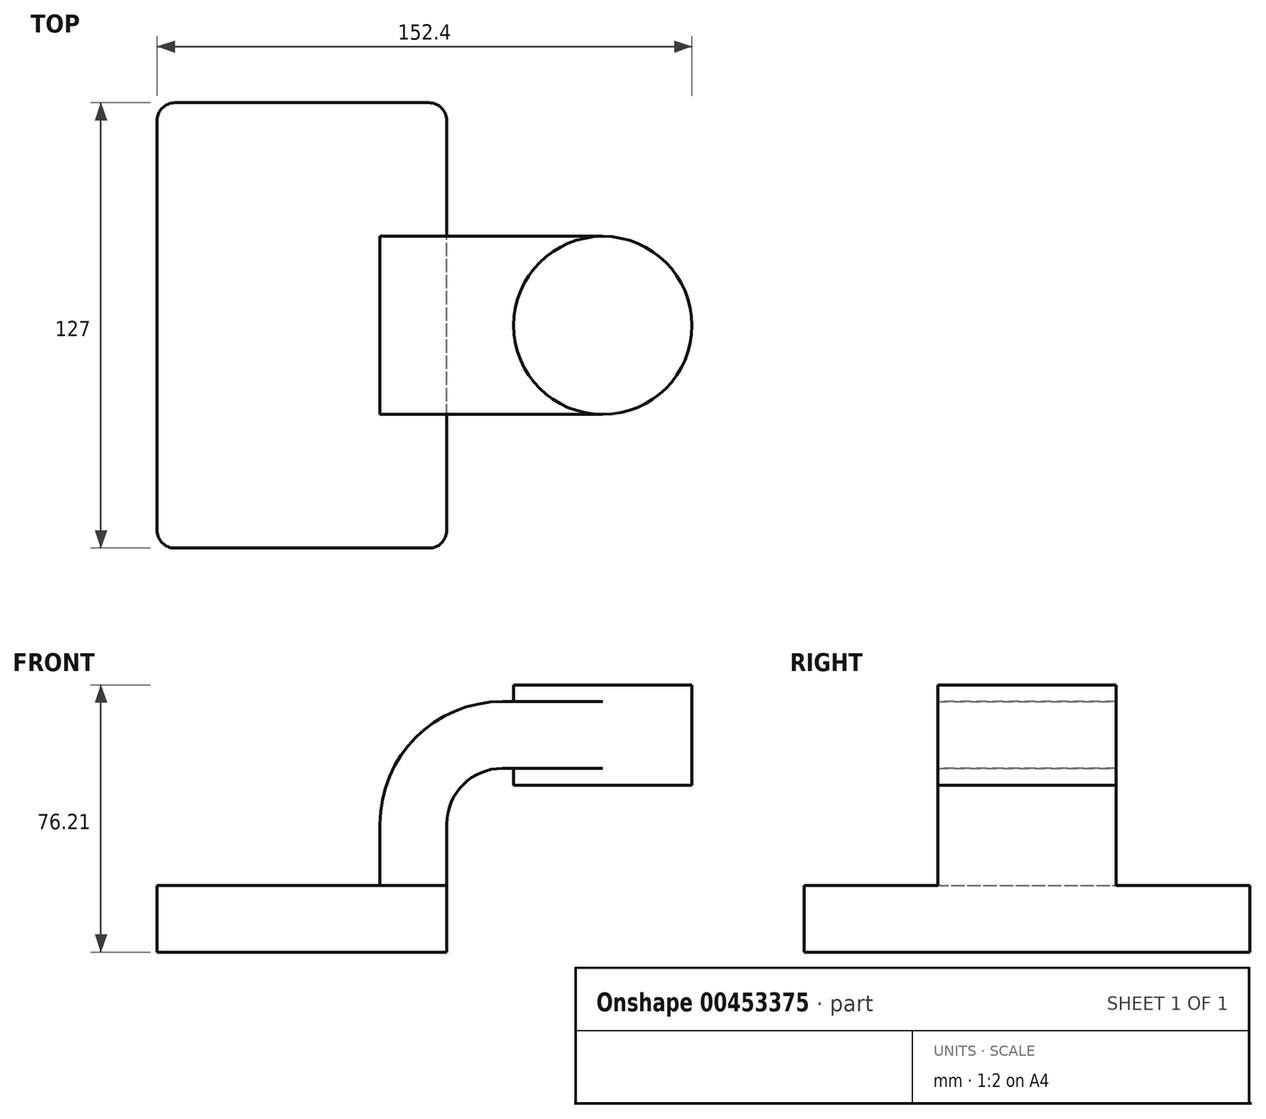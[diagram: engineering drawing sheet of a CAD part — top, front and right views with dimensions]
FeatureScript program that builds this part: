
annotation { "Feature Type Name" : "Feature", "Feature Type Description" : "" }
export const myFeature = defineFeature(function(context is Context, id is Id, definition is map)
    precondition{}
    {
        {
            var Q0;
            Q0=qCreatedBy(makeId("Front.planeOp"),FACE);
            var sketch = newSketch(context, id + "F0", { "sketchPlane" : qUnion([Q0])});
            skLineSegment(sketch, "E0.bottom", {"start": v(-41.28, -9.53) * mm, "end": v(41.28, -9.53) * mm});
            skLineSegment(sketch, "E0.top", {"start": v(-41.28, 9.53) * mm, "end": v(41.28, 9.53) * mm});
            skLineSegment(sketch, "E0.left", {"start": v(-41.28, -9.53) * mm, "end": v(-41.28, 9.53) * mm});
            skLineSegment(sketch, "E0.right", {"start": v(41.28, -9.53) * mm, "end": v(41.28, 9.52) * mm});
            skPoint(sketch, "E0.middle", {"position": v(0, 0) * mm});
            skLineSegment(sketch, "E1.bottom", {"start": v(111.13, 38.1) * mm, "end": v(60.33, 38.1) * mm});
            skLineSegment(sketch, "E1.top", {"start": v(111.13, 66.68) * mm, "end": v(60.33, 66.68) * mm});
            skLineSegment(sketch, "E1.left", {"start": v(111.13, 38.1) * mm, "end": v(111.13, 66.68) * mm});
            skLineSegment(sketch, "E1.right", {"start": v(60.33, 38.1) * mm, "end": v(60.33, 66.67) * mm});
            skPoint(sketch, "E1.middle", {"position": v(85.73, 52.39) * mm});
            skLineSegment(sketch, "E2", {"start": v(41.28, 9.52) * mm, "end": v(41.28, 27) * mm});
            skArc(sketch, "E3", {"start": v(41.27, 27) * mm, "mid": v(45.92, 38.23) * mm, "end": v(57.15, 42.88) * mm});
            skLineSegment(sketch, "E4", {"start": v(57.15, 42.88) * mm, "end": v(77.2, 42.88) * mm});
            skLineSegment(sketch, "E5.0", {"start": v(57.15, 61.93) * mm, "end": v(77.2, 61.93) * mm});
            skArc(sketch, "E5.1", {"start": v(22.22, 27) * mm, "mid": v(32.45, 51.7) * mm, "end": v(57.15, 61.93) * mm});
            skLineSegment(sketch, "E5.2", {"start": v(22.22, 9.52) * mm, "end": v(22.22, 27) * mm});
            skLineSegment(sketch, "E6", {"start": v(77.2, 42.88) * mm, "end": v(85.73, 42.88) * mm});
            skPoint(sketch, "E6.endSnap0", {"position": v(85.73, 38.1) * mm});
            skLineSegment(sketch, "E7", {"start": v(77.2, 61.93) * mm, "end": v(85.73, 61.93) * mm});
            skLineSegment(sketch, "E8", {"start": v(85.73, 66.68) * mm, "end": v(85.73, 38.1) * mm});
            skFitSpline(sketch, "E9", {"points": [v(-41.28, 9.53) * mm, v(57.15, 61.93) * mm], "startDerivative": vector(1.62, 75.65) * mm, "endDerivative": vector(129.34, 0) * mm});
            skSolve(sketch);
        }
        {
            var Q0;
            Q0=makeQuery(id+"F0.imprint","IMPRINT",FACE,{"disambiguationData":[TD([[makeQuery(id+"F0.imprint","IMPRINT",EDGE,{"derivedFrom":sQuery(id+"F0.wireOp",EDGE,"E0.bottom")}),1.0]])]});
            extrude(context, id + "F1", {"entities" : qUnion([Q0]), "endBound" : BoundingType.SYMMETRIC, "depth" : 127 * mm});
        }
        {
            var Q0;
            {var subQ1=sQuery(id+"F0.wireOp",EDGE,"E2");Q0=makeQuery(id+"F0.imprint","IMPRINT",FACE,{"disambiguationData":[TD([[makeQuery(id+"F0.imprint","IMPRINT",EDGE,{"derivedFrom":subQ1}),1.0]])]});}
            var Q1;
            {var subQ4=sQuery(id+"F0.wireOp",EDGE,"E6");Q1=makeQuery(id+"F0.imprint","IMPRINT",FACE,{"disambiguationData":[TD([[makeQuery(id+"F0.imprint","IMPRINT",EDGE,{"derivedFrom":subQ4}),1.0]])]});}
            extrude(context, id + "F2", {"entities" : qUnion([Q0, Q1]), "operationType" : NewBodyOperationType.ADD, "endBound" : BoundingType.SYMMETRIC, "depth" : 50.8 * mm});
        }
        {
            var Q0;
            Q0=makeQuery(id+"F0.imprint","IMPRINT",FACE,{"disambiguationData":[TD([[makeQuery(id+"F0.imprint","IMPRINT",EDGE,{"derivedFrom":sQuery(id+"F0.wireOp",EDGE,"E5.1")}),1.0]])]});
            extrude(context, id + "F3", {"entities" : qUnion([Q0]), "operationType" : NewBodyOperationType.ADD, "endBound" : BoundingType.SYMMETRIC, "depth" : 25.4 * mm});
        }
        {
            var Q0;
            {var subQ4=sQuery(id+"F0.wireOp",EDGE,"E1.left");Q0=makeQuery(id+"F0.imprint","IMPRINT",FACE,{"disambiguationData":[TD([[makeQuery(id+"F0.imprint","IMPRINT",EDGE,{"derivedFrom":subQ4}),1.0]])]});}
            var Q1;
            Q1=sQuery(id+"F0.wireOp",EDGE,"E8");
            revolve(context, id + "F4", {"operationType" : NewBodyOperationType.ADD, "entities" : qUnion([Q0]), "axis" : qUnion([Q1]), "revolveType" : RevolveType.FULL});
        }
        {
            var Q0;
            Q0=makeQuery(id+"F1.opExtrude","CAP_EDGE",EDGE,{"disambiguationData":[OSD([sQuery(id+"F0.wireOp",EDGE,"E0.right")])],"isStart":false});
            var Q1;
            Q1=makeQuery(id+"F1.opExtrude","CAP_EDGE",EDGE,{"disambiguationData":[OSD([sQuery(id+"F0.wireOp",EDGE,"E0.left")])],"isStart":false});
            var Q2;
            Q2=makeQuery(id+"F1.opExtrude","CAP_EDGE",EDGE,{"disambiguationData":[OSD([sQuery(id+"F0.wireOp",EDGE,"E0.right")])],"isStart":true});
            var Q3;
            Q3=makeQuery(id+"F1.opExtrude","CAP_EDGE",EDGE,{"disambiguationData":[OSD([sQuery(id+"F0.wireOp",EDGE,"E0.left")])],"isStart":true});
            fillet(context, id + "F5", {"entities" : qUnion([Q0, Q1, Q2, Q3]), "radius" : 5.08 * mm, "tangentPropagation" : true, "allowEdgeOverflow" : false});
        }
    });
